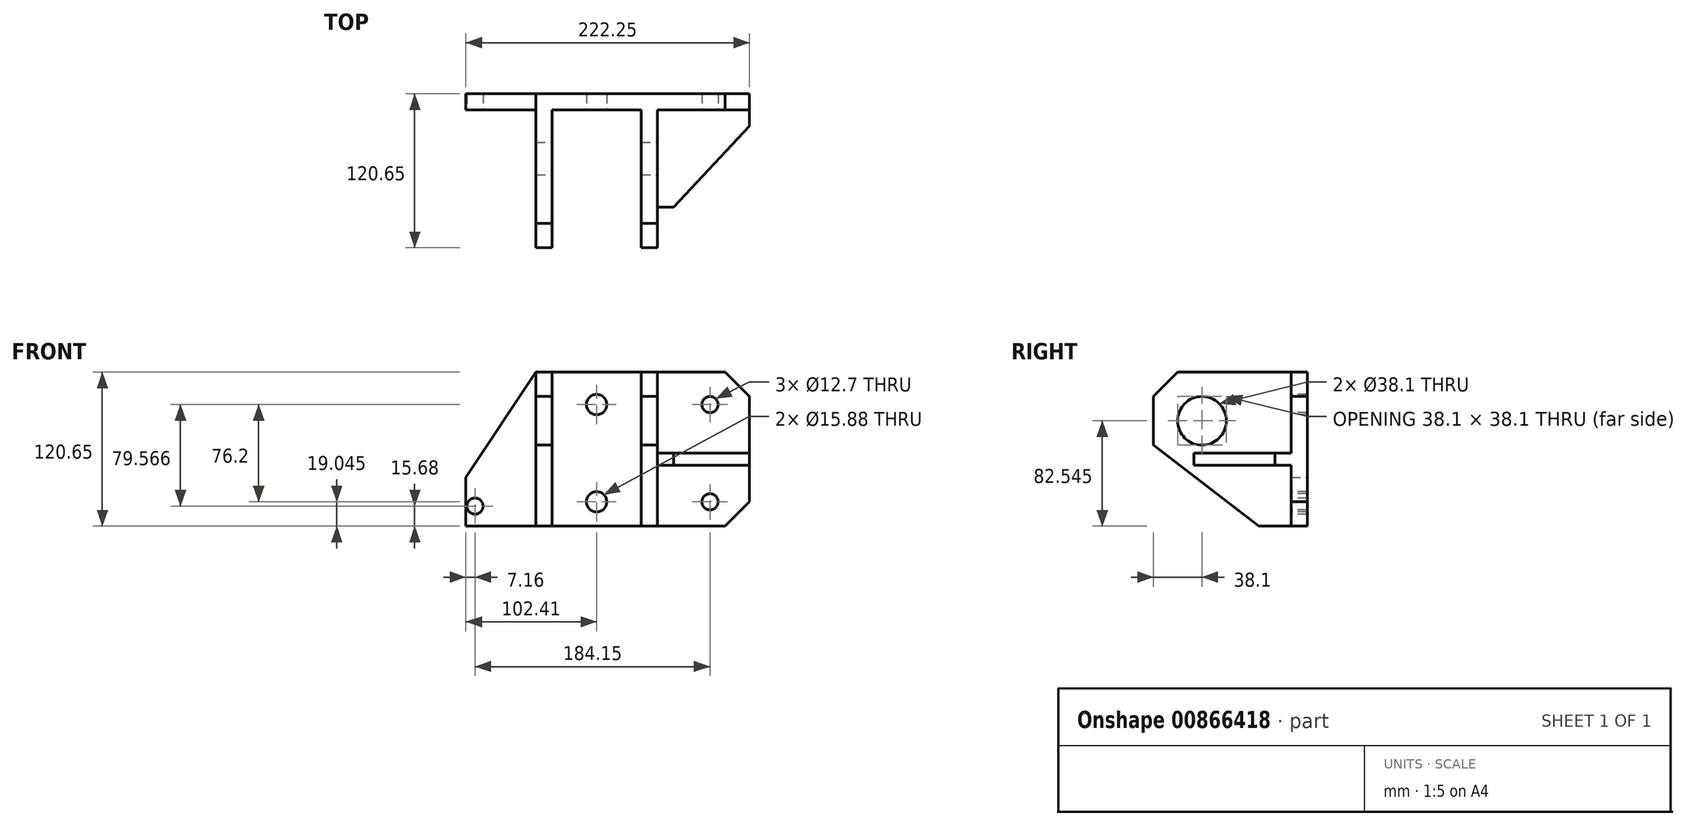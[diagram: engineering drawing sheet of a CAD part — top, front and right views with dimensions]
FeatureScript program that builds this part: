
annotation { "Feature Type Name" : "Feature", "Feature Type Description" : "" }
export const myFeature = defineFeature(function(context is Context, id is Id, definition is map)
    precondition{}
    {
        {
            var Q0;
            Q0=qCreatedBy(makeId("Front.planeOp"),FACE);
            var sketch = newSketch(context, id + "F0", { "sketchPlane" : qUnion([Q0])});
            skLineSegment(sketch, "E0.bottom", {"start": v(-58.38, 47.39) * mm, "end": v(109.08, 47.39) * mm});
            skLineSegment(sketch, "E0.top", {"start": v(-113.17, -73.26) * mm, "end": v(109.08, -73.26) * mm});
            skLineSegment(sketch, "E0.left", {"start": v(-113.17, -35.16) * mm, "end": v(-113.17, -73.26) * mm});
            skLineSegment(sketch, "E0.right", {"start": v(109.08, 47.39) * mm, "end": v(109.08, -73.26) * mm});
            skLineSegment(sketch, "E1", {"start": v(-113.17, -35.16) * mm, "end": v(-58.38, 47.39) * mm});
            skSolve(sketch);
        }
        {
            var Q0;
            Q0 = qSketchRegion(id + "F0", true);
            extrude(context, id + "F1", {"entities" : qUnion([Q0]), "depth" : 12.7 * mm, "offsetDistance" : 25.4 * mm});
        }
        {
            var Q0;
            Q0=makeQuery(id+"F1.opExtrude","SWEPT_EDGE",EDGE,{"disambiguationData":[OSD([sQuery(id+"F0.wireOp",EDGE,"E0.top"),sQuery(id+"F0.wireOp",EDGE,"E0.right")])]});
            var Q1;
            Q1=makeQuery(id+"F1.opExtrude","SWEPT_EDGE",EDGE,{"disambiguationData":[OSD([sQuery(id+"F0.wireOp",EDGE,"E0.bottom"),sQuery(id+"F0.wireOp",EDGE,"E0.right")])]});
            chamfer(context, id + "F2", {"entities" : qUnion([Q0, Q1]), "width" : 19.05 * mm, "tangentPropagation" : true});
        }
        {
            var Q0;
            Q0=makeQuery(id+"F1.opExtrude","CAP_FACE",FACE,{"disambiguationData":[OSD([sQuery(id+"F0.wireOp",EDGE,"E0.bottom"),sQuery(id+"F0.wireOp",EDGE,"E0.top"),sQuery(id+"F0.wireOp",EDGE,"E0.left"),sQuery(id+"F0.wireOp",EDGE,"E0.right"),sQuery(id+"F0.wireOp",EDGE,"E1")])],"isStart":false});
            var sketch = newSketch(context, id + "F3", { "sketchPlane" : qUnion([Q0])});
            skLineSegment(sketch, "E2", {"start": v(-58.38, 47.39) * mm, "end": v(-58.38, -73.26) * mm});
            skLineSegment(sketch, "E3", {"start": v(-58.38, -73.26) * mm, "end": v(-45.68, -73.26) * mm});
            skLineSegment(sketch, "E4", {"start": v(-45.68, -73.26) * mm, "end": v(-45.68, 47.39) * mm});
            skLineSegment(sketch, "E5", {"start": v(-45.68, 47.39) * mm, "end": v(-58.38, 47.39) * mm});
            skLineSegment(sketch, "E6", {"start": v(24.17, -73.26) * mm, "end": v(36.87, -73.26) * mm});
            skLineSegment(sketch, "E7", {"start": v(36.87, -73.26) * mm, "end": v(36.87, 47.39) * mm});
            skLineSegment(sketch, "E8", {"start": v(24.17, -73.26) * mm, "end": v(24.17, 47.39) * mm});
            skLineSegment(sketch, "E9", {"start": v(24.17, 47.39) * mm, "end": v(36.87, 47.39) * mm});
            skCircle(sketch, "E10", {"center": v(-106, -57.58) * mm, "radius": 6.35 * mm});
            skLineSegment(sketch, "E11", {"start": v(36.87, -25.64) * mm, "end": v(109.08, -25.64) * mm});
            skLineSegment(sketch, "E12", {"start": v(109.08, -25.64) * mm, "end": v(109.08, -16.11) * mm});
            skLineSegment(sketch, "E13", {"start": v(109.08, -16.11) * mm, "end": v(36.87, -16.11) * mm});
            skCircle(sketch, "E14", {"center": v(-10.76, -54.21) * mm, "radius": 7.94 * mm});
            skCircle(sketch, "E15", {"center": v(-10.76, 21.99) * mm, "radius": 7.94 * mm});
            skCircle(sketch, "E16", {"center": v(78.14, 21.99) * mm, "radius": 6.35 * mm});
            skCircle(sketch, "E17", {"center": v(78.14, -54.21) * mm, "radius": 6.35 * mm});
            skSolve(sketch);
        }
        {
            var Q0;
            Q0=makeQuery(id+"F3.imprint","IMPRINT",FACE,{"disambiguationData":[TD([[makeQuery(id+"F3.imprint","IMPRINT",EDGE,{"derivedFrom":sQuery(id+"F3.wireOp",EDGE,"E15")}),1.0]])]});
            var Q1;
            Q1=makeQuery(id+"F3.imprint","IMPRINT",FACE,{"disambiguationData":[TD([[makeQuery(id+"F3.imprint","IMPRINT",EDGE,{"derivedFrom":sQuery(id+"F3.wireOp",EDGE,"E16")}),1.0]])]});
            var Q2;
            Q2=makeQuery(id+"F3.imprint","IMPRINT",FACE,{"disambiguationData":[TD([[makeQuery(id+"F3.imprint","IMPRINT",EDGE,{"derivedFrom":sQuery(id+"F3.wireOp",EDGE,"E17")}),1.0]])]});
            var Q3;
            Q3=makeQuery(id+"F3.imprint","IMPRINT",FACE,{"disambiguationData":[TD([[makeQuery(id+"F3.imprint","IMPRINT",EDGE,{"derivedFrom":sQuery(id+"F3.wireOp",EDGE,"E10")}),1.0]])]});
            var Q4;
            Q4=makeQuery(id+"F3.imprint","IMPRINT",FACE,{"disambiguationData":[TD([[makeQuery(id+"F3.imprint","IMPRINT",EDGE,{"derivedFrom":sQuery(id+"F3.wireOp",EDGE,"E14")}),1.0]])]});
            extrude(context, id + "F4", {"entities" : qUnion([Q0, Q1, Q2, Q3, Q4]), "operationType" : NewBodyOperationType.REMOVE, "oppositeDirection" : true, "depth" : 74.42 * mm, "offsetDistance" : 25.4 * mm});
        }
        {
            var Q0;
            Q0=makeQuery(id+"F3.imprint","IMPRINT",FACE,{"disambiguationData":[TD([[makeQuery(id+"F3.imprint","IMPRINT",EDGE,{"derivedFrom":sQuery(id+"F3.wireOp",EDGE,"E2")}),1.0]])]});
            var Q1;
            {var subQ4=sQuery(id+"F3.wireOp",EDGE,"E6");Q1=makeQuery(id+"F3.imprint","IMPRINT",FACE,{"disambiguationData":[TD([[makeQuery(id+"F3.imprint","IMPRINT",EDGE,{"derivedFrom":subQ4}),1.0]])]});}
            extrude(context, id + "F5", {"entities" : qUnion([Q0, Q1]), "operationType" : NewBodyOperationType.ADD, "depth" : 107.95 * mm, "offsetDistance" : 25.4 * mm});
        }
        {
            var Q0;
            Q0=makeQuery(id+"F5.opExtrude","CAP_EDGE",EDGE,{"disambiguationData":[OSD([sQuery(id+"F3.wireOp",EDGE,"E9")])],"isStart":false});
            var Q1;
            Q1=makeQuery(id+"F5.opExtrude","CAP_EDGE",EDGE,{"disambiguationData":[OSD([sQuery(id+"F3.wireOp",EDGE,"E5")])],"isStart":false});
            chamfer(context, id + "F6", {"entities" : qUnion([Q0, Q1]), "width" : 19.05 * mm, "tangentPropagation" : true});
        }
        {
            var Q0;
            Q0=makeQuery(id+"F5.opExtrude","SWEPT_FACE",FACE,{"disambiguationData":[OSD([sQuery(id+"F3.wireOp",EDGE,"E7")])]});
            var sketch = newSketch(context, id + "F7", { "sketchPlane" : qUnion([Q0])});
            skLineSegment(sketch, "E18", {"start": v(-120.65, -9.76) * mm, "end": v(-38.1, -73.26) * mm});
            skCircle(sketch, "E19", {"center": v(-82.55, 9.29) * mm, "radius": 19.05 * mm});
            skSolve(sketch);
        }
        {
            var Q0;
            Q0 = qSketchRegion(id + "F7", true);
            var Q1;
            {var subQ0=sQuery(id+"F7.wireOp",EDGE,"E18");Q1=makeQuery(id+"F7.imprint","IMPRINT",FACE,{"disambiguationData":[TD([[makeQuery(id+"F7.imprint","IMPRINT",EDGE,{"derivedFrom":subQ0}),-1.0]])]});}
            extrude(context, id + "F8", {"entities" : qUnion([Q0, Q1]), "operationType" : NewBodyOperationType.REMOVE, "oppositeDirection" : true, "depth" : 399.03 * mm, "offsetDistance" : 25.4 * mm});
        }
        {
            var Q0;
            {var subQ0=sQuery(id+"F3.wireOp",EDGE,"E11");Q0=makeQuery(id+"F3.imprint","IMPRINT",FACE,{"disambiguationData":[TD([[makeQuery(id+"F3.imprint","IMPRINT",EDGE,{"derivedFrom":subQ0}),1.0]])]});}
            extrude(context, id + "F9", {"entities" : qUnion([Q0]), "operationType" : NewBodyOperationType.ADD, "depth" : 76.2 * mm, "offsetDistance" : 25.4 * mm});
        }
        {
            var Q0;
            Q0=makeQuery(id+"F9.opExtrude","SWEPT_FACE",FACE,{"disambiguationData":[OSD([sQuery(id+"F3.wireOp",EDGE,"E11")])]});
            var sketch = newSketch(context, id + "F10", { "sketchPlane" : qUnion([Q0])});
            skLineSegment(sketch, "E20", {"start": v(49.57, 88.9) * mm, "end": v(109.08, 25.4) * mm});
            skSolve(sketch);
        }
        {
            var Q0;
            Q0 = qSketchRegion(id + "F10", true);
            var Q1;
            {var subQ0=sQuery(id+"F10.wireOp",EDGE,"E20");Q1=makeQuery(id+"F10.imprint","IMPRINT",FACE,{"disambiguationData":[TD([[makeQuery(id+"F10.imprint","IMPRINT",EDGE,{"derivedFrom":subQ0}),1.0]])]});}
            extrude(context, id + "F11", {"entities" : qUnion([Q0, Q1]), "operationType" : NewBodyOperationType.REMOVE, "oppositeDirection" : true, "depth" : 180.85 * mm, "offsetDistance" : 25.4 * mm});
        }
    });
